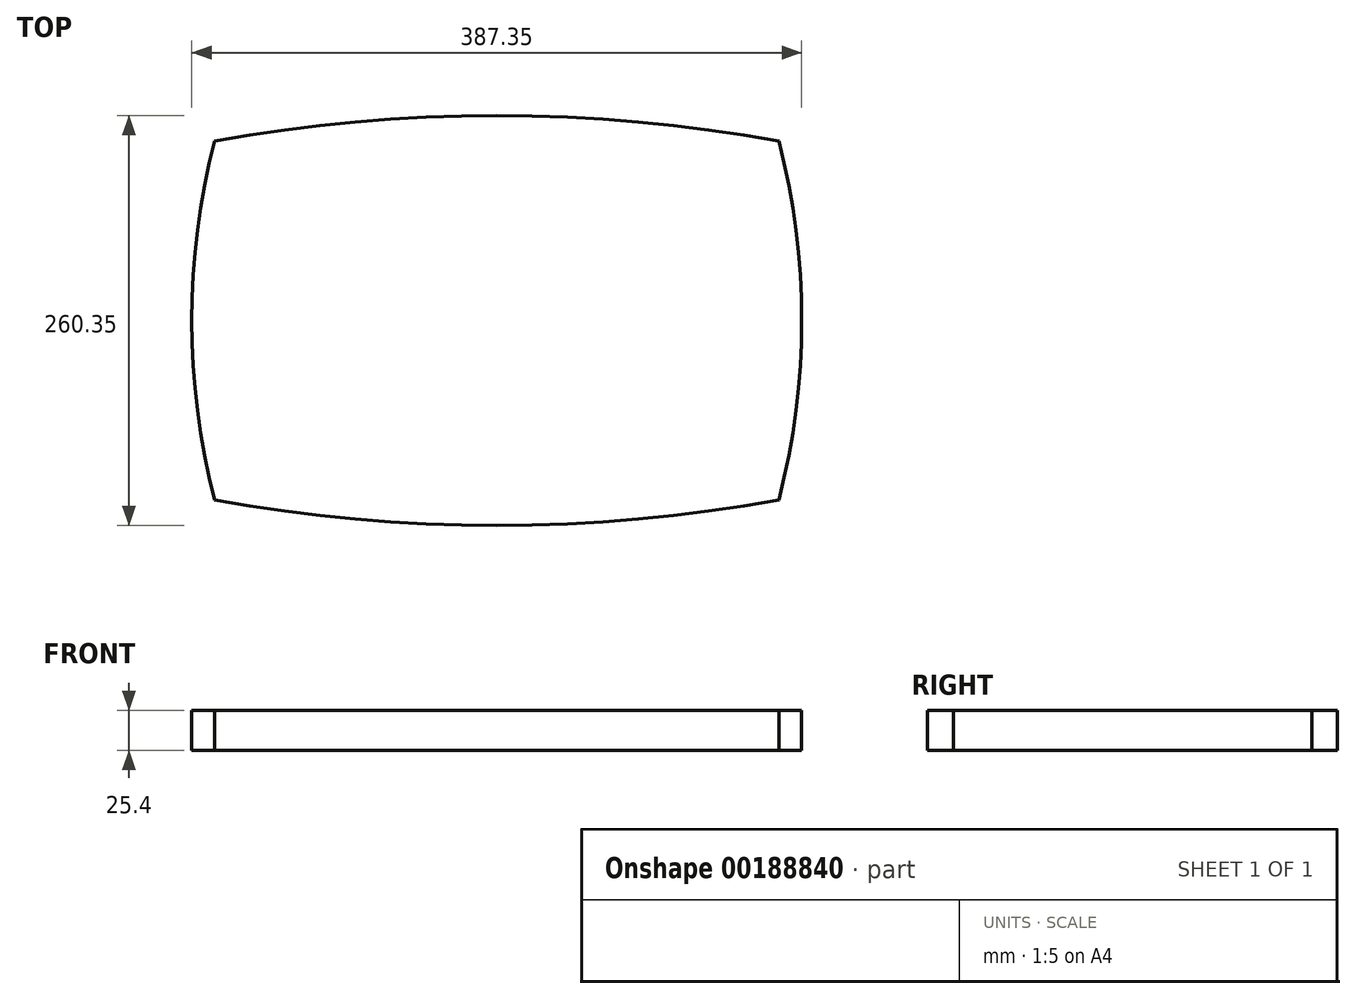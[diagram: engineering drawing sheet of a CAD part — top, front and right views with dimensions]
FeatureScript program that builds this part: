
annotation { "Feature Type Name" : "Feature", "Feature Type Description" : "" }
export const myFeature = defineFeature(function(context is Context, id is Id, definition is map)
    precondition{}
    {
        {
            var Q0;
            Q0=qCreatedBy(makeId("Top.planeOp"),FACE);
            var sketch = newSketch(context, id + "F0", { "sketchPlane" : qUnion([Q0])});
            skLineSegment(sketch, "E0", {"start": v(0, 130.18) * mm, "end": v(387.35, 130.18) * mm, "construction": true});
            skLineSegment(sketch, "E1", {"start": v(193.67, 260.35) * mm, "end": v(193.67, 0) * mm, "construction": true});
            skLineSegment(sketch, "E2", {"start": v(19.05, 260.35) * mm, "end": v(19.05, 0) * mm, "construction": true});
            skLineSegment(sketch, "E3", {"start": v(13.8, 241.3) * mm, "end": v(387.35, 241.3) * mm, "construction": true});
            skLineSegment(sketch, "E4", {"start": v(411.31, 19.05) * mm, "end": v(-43.06, 19.05) * mm, "construction": true});
            skArc(sketch, "E5", {"start": v(14.5, 244.07) * mm, "mid": v(0, 130.17) * mm, "end": v(14.5, 16.28) * mm});
            skArc(sketch, "E6", {"start": v(372.84, 16.28) * mm, "mid": v(387.35, 130.18) * mm, "end": v(372.84, 244.07) * mm});
            skArc(sketch, "E7", {"start": v(14.5, 16.28) * mm, "mid": v(193.67, 0) * mm, "end": v(372.84, 16.28) * mm});
            skArc(sketch, "E8", {"start": v(387.35, 241.3) * mm, "mid": v(201.06, 260.32) * mm, "end": v(14.5, 244.07) * mm});
            skPoint(sketch, "E9.top.start.orphan", {"position": v(0, 260.35) * mm});
            skPoint(sketch, "E10.orphan", {"position": v(0, 0) * mm});
            skPoint(sketch, "E11.orphan", {"position": v(387.35, 19.05) * mm});
            skLineSegment(sketch, "E12.trimOffspring", {"start": v(368.3, 244.9) * mm, "end": v(368.3, -56.82) * mm, "construction": true});
            skPoint(sketch, "E9.right.end.orphan", {"position": v(387.35, 260.35) * mm});
            skPoint(sketch, "E9.bottom.end.orphan", {"position": v(387.35, 0) * mm});
            skSolve(sketch);
        }
        {
            var Q0;
            Q0 = qSketchRegion(id + "F0", true);
            extrude(context, id + "F1", {"entities" : qUnion([Q0]), "depth" : 25.4 * mm});
        }
    });
